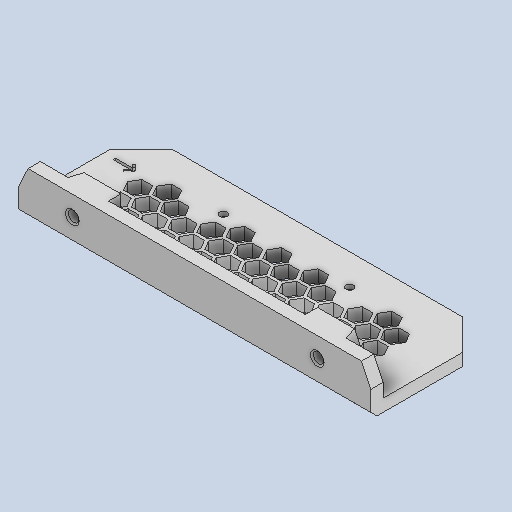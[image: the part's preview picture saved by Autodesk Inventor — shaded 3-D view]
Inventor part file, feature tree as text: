
AUTODESK INVENTOR PART (.ipt)
format: ipt  version: 2023 (Build 270158000, 158)  size: 583,168 bytes
history: native  units: in
note: dims shown in document units (in); Inventor stores cm internally (conversion verified against a paired STEP export)
features: sketch x4, other x3
ambient origin geometry x8: Origin, YZ Plane, XZ Plane, XY Plane, X Axis, Y Axis, Z Axis, Center Point
bodies: Solid1 (feature_tree)
feature tree (7):
  other  "A-01.ipt"
  other  "Solid1::A-01.ipt"
  other  "TaggingFeature1"
  sketch  "Sketch1"  dims[d0=0.3937in]
  sketch  "Sketch4"
  sketch  "Sketch5"
  sketch  "Sketch6"
